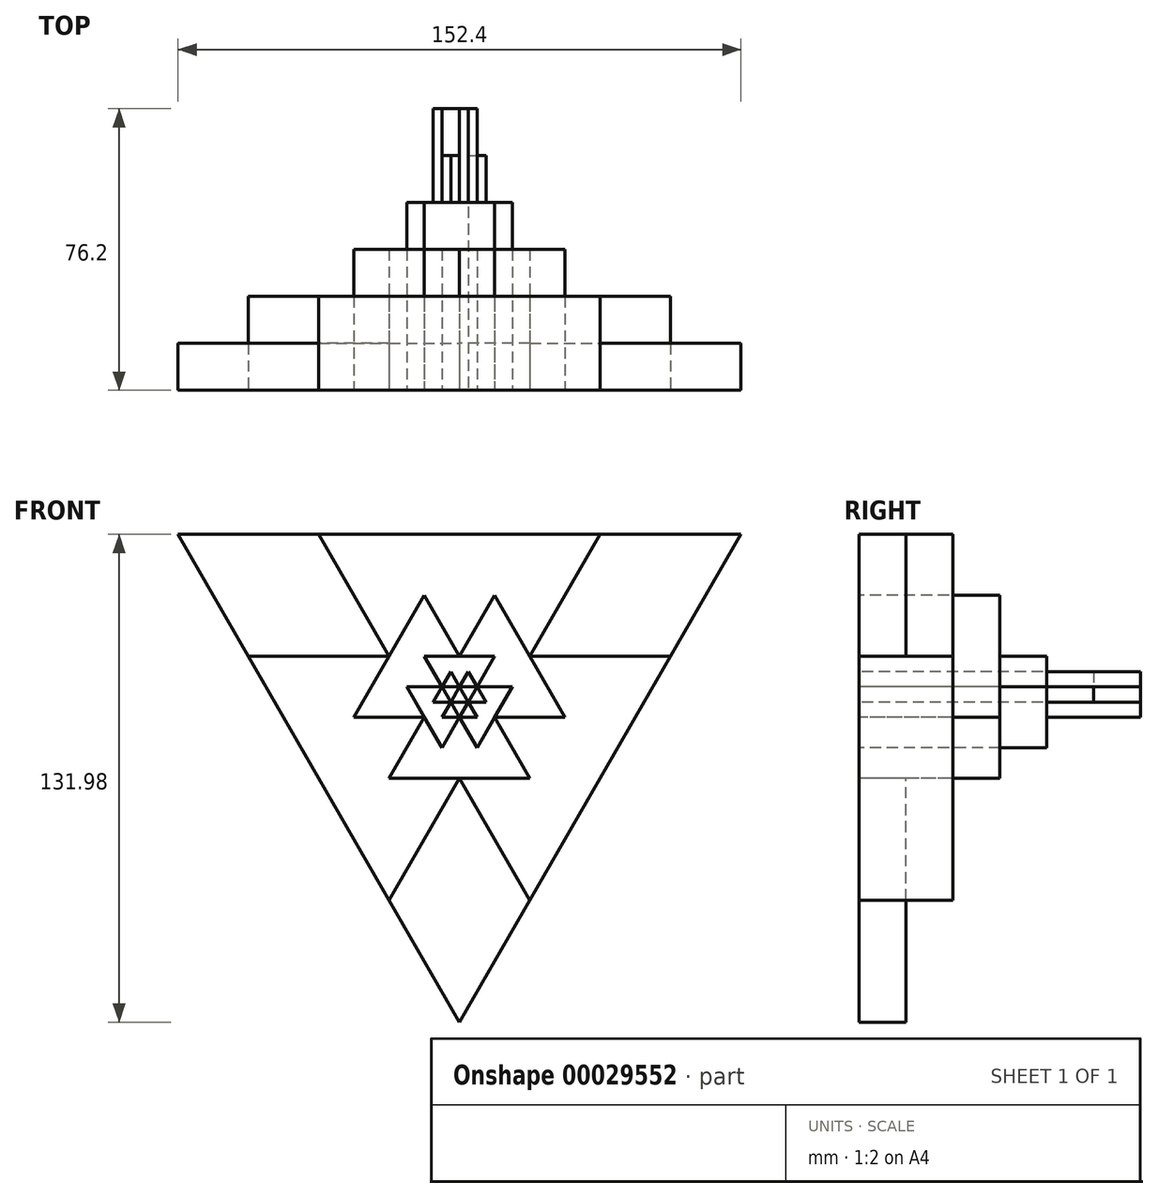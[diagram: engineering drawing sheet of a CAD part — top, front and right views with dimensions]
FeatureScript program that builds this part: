
annotation { "Feature Type Name" : "Feature", "Feature Type Description" : "" }
export const myFeature = defineFeature(function(context is Context, id is Id, definition is map)
    precondition{}
    {
        {
            var Q0;
            Q0=qCreatedBy(makeId("Front.planeOp"),FACE);
            var sketch = newSketch(context, id + "F0", { "sketchPlane" : qUnion([Q0])});
            skLineSegment(sketch, "E0.0", {"start": v(-76.2, 44) * mm, "end": v(76.2, 44) * mm});
            skLineSegment(sketch, "E0.1", {"start": v(76.2, 44) * mm, "end": v(0, -87.99) * mm});
            skLineSegment(sketch, "E0.2", {"start": v(0, -87.99) * mm, "end": v(-76.2, 44) * mm});
            skPoint(sketch, "E0.0.midPoint", {"position": v(0, 44) * mm});
            skLineSegment(sketch, "E1", {"start": v(-38.1, -22) * mm, "end": v(0, 44) * mm});
            skLineSegment(sketch, "E2", {"start": v(38.1, -22) * mm, "end": v(0, 44) * mm});
            skLineSegment(sketch, "E3", {"start": v(-38.1, -22) * mm, "end": v(38.1, -22) * mm});
            skLineSegment(sketch, "E4", {"start": v(0, -87.99) * mm, "end": v(-38.1, -22) * mm});
            skLineSegment(sketch, "E5", {"start": v(0, -87.99) * mm, "end": v(38.1, -22) * mm});
            skLineSegment(sketch, "E6", {"start": v(-76.2, 44) * mm, "end": v(-38.1, -22) * mm});
            skLineSegment(sketch, "E7", {"start": v(-76.2, 44) * mm, "end": v(0, 44) * mm});
            skLineSegment(sketch, "E8", {"start": v(0, 44) * mm, "end": v(76.2, 44) * mm});
            skLineSegment(sketch, "E9", {"start": v(38.1, -22) * mm, "end": v(76.2, 44) * mm});
            skPoint(sketch, "E0.cCircle.center.orphan", {"position": v(0, 0) * mm});
            skLineSegment(sketch, "E10", {"start": v(-19.05, 11) * mm, "end": v(19.05, 11) * mm});
            skLineSegment(sketch, "E11", {"start": v(0, -22) * mm, "end": v(19.05, 11) * mm});
            skLineSegment(sketch, "E12", {"start": v(-19.05, 11) * mm, "end": v(0, -22) * mm});
            skLineSegment(sketch, "E13", {"start": v(-9.52, -5.5) * mm, "end": v(-19.05, -22) * mm});
            skLineSegment(sketch, "E14", {"start": v(-9.52, -5.5) * mm, "end": v(-28.57, -5.5) * mm});
            skLineSegment(sketch, "E15", {"start": v(-28.57, -5.5) * mm, "end": v(-19.05, -22) * mm});
            skLineSegment(sketch, "E16", {"start": v(9.53, -5.5) * mm, "end": v(28.58, -5.5) * mm});
            skLineSegment(sketch, "E17", {"start": v(28.58, -5.5) * mm, "end": v(19.05, -22) * mm});
            skLineSegment(sketch, "E18", {"start": v(19.05, -22) * mm, "end": v(9.52, -5.5) * mm});
            skPoint(sketch, "E19.start.orphan", {"position": v(0, 11) * mm});
            skLineSegment(sketch, "E20", {"start": v(0, 11) * mm, "end": v(-9.52, 27.5) * mm});
            skLineSegment(sketch, "E21", {"start": v(-9.52, 27.5) * mm, "end": v(9.52, 27.5) * mm});
            skLineSegment(sketch, "E22", {"start": v(9.52, 27.5) * mm, "end": v(0, 11) * mm});
            skPoint(sketch, "E23.start.orphan", {"position": v(-9.52, -38.5) * mm});
            skPoint(sketch, "E24.end.orphan", {"position": v(9.53, -38.5) * mm});
            skPoint(sketch, "E24.start.orphan", {"position": v(0, -55) * mm});
            skPoint(sketch, "E25.end.orphan", {"position": v(-47.62, 27.5) * mm});
            skPoint(sketch, "E26.end.orphan", {"position": v(-28.57, 27.5) * mm});
            skPoint(sketch, "E26.start.orphan", {"position": v(-38.1, 11) * mm});
            skPoint(sketch, "E27.orphan", {"position": v(-57.15, 11) * mm});
            skPoint(sketch, "E28.orphan", {"position": v(-38.1, 44) * mm});
            skPoint(sketch, "E29.end.orphan", {"position": v(47.62, 27.5) * mm});
            skPoint(sketch, "E29.start.orphan", {"position": v(38.1, 11) * mm});
            skPoint(sketch, "E30.orphan", {"position": v(57.15, 11) * mm});
            skPoint(sketch, "E31.start.orphan", {"position": v(38.1, 44) * mm});
            skPoint(sketch, "E32.end.orphan", {"position": v(28.57, 27.5) * mm});
            skPoint(sketch, "E33.orphan", {"position": v(19.05, -55) * mm});
            skPoint(sketch, "E34.start.orphan", {"position": v(-19.05, -55) * mm});
            skLineSegment(sketch, "E35", {"start": v(-38.1, 44) * mm, "end": v(-57.15, 11) * mm});
            skLineSegment(sketch, "E36", {"start": v(-19.05, 11) * mm, "end": v(-57.15, 11) * mm});
            skLineSegment(sketch, "E37", {"start": v(-38.1, 44) * mm, "end": v(-19.05, 11) * mm});
            skLineSegment(sketch, "E38", {"start": v(19.05, 11) * mm, "end": v(38.1, 44) * mm});
            skLineSegment(sketch, "E39", {"start": v(57.15, 11) * mm, "end": v(38.1, 44) * mm});
            skLineSegment(sketch, "E40", {"start": v(19.05, 11) * mm, "end": v(57.15, 11) * mm});
            skLineSegment(sketch, "E41", {"start": v(-19.05, -55) * mm, "end": v(0, -22) * mm});
            skLineSegment(sketch, "E42", {"start": v(19.05, -55) * mm, "end": v(0, -22) * mm});
            skLineSegment(sketch, "E43", {"start": v(-19.05, -55) * mm, "end": v(19.05, -55) * mm});
            skLineSegment(sketch, "E44", {"start": v(-9.52, -5.5) * mm, "end": v(0, 11) * mm});
            skLineSegment(sketch, "E45", {"start": v(9.53, -5.5) * mm, "end": v(0, 11) * mm});
            skLineSegment(sketch, "E46", {"start": v(-9.52, -5.5) * mm, "end": v(9.53, -5.5) * mm});
            skLineSegment(sketch, "E47", {"start": v(-4.76, 2.75) * mm, "end": v(0, -5.5) * mm});
            skLineSegment(sketch, "E48", {"start": v(0, -5.5) * mm, "end": v(4.76, 2.75) * mm});
            skLineSegment(sketch, "E49", {"start": v(4.76, 2.75) * mm, "end": v(-4.76, 2.75) * mm});
            skLineSegment(sketch, "E50", {"start": v(0, -5.5) * mm, "end": v(4.76, -13.75) * mm});
            skLineSegment(sketch, "E51", {"start": v(4.76, -13.75) * mm, "end": v(-4.76, -13.75) * mm});
            skLineSegment(sketch, "E52", {"start": v(-4.76, -13.75) * mm, "end": v(0, -5.5) * mm});
            skLineSegment(sketch, "E53", {"start": v(-4.76, 2.75) * mm, "end": v(-9.52, 11) * mm});
            skLineSegment(sketch, "E54", {"start": v(-4.76, 2.75) * mm, "end": v(-14.29, 2.75) * mm});
            skLineSegment(sketch, "E55", {"start": v(-14.29, 2.75) * mm, "end": v(-9.52, 11) * mm});
            skLineSegment(sketch, "E56", {"start": v(4.76, 2.75) * mm, "end": v(14.29, 2.75) * mm});
            skLineSegment(sketch, "E57", {"start": v(4.76, 2.75) * mm, "end": v(9.53, 11) * mm});
            skLineSegment(sketch, "E58", {"start": v(9.53, 11) * mm, "end": v(14.29, 2.75) * mm});
            skLineSegment(sketch, "E59", {"start": v(-2.38, -1.37) * mm, "end": v(-4.76, -5.5) * mm});
            skLineSegment(sketch, "E60", {"start": v(-2.38, -1.37) * mm, "end": v(-7.14, -1.37) * mm});
            skLineSegment(sketch, "E61", {"start": v(-7.14, -1.37) * mm, "end": v(-4.76, -5.5) * mm});
            skLineSegment(sketch, "E62", {"start": v(2.38, -1.37) * mm, "end": v(7.14, -1.37) * mm});
            skLineSegment(sketch, "E63", {"start": v(7.14, -1.37) * mm, "end": v(4.76, -5.5) * mm});
            skLineSegment(sketch, "E64", {"start": v(4.76, -5.5) * mm, "end": v(2.38, -1.37) * mm});
            skLineSegment(sketch, "E65", {"start": v(0, 2.75) * mm, "end": v(2.38, 6.87) * mm});
            skLineSegment(sketch, "E66", {"start": v(2.38, 6.87) * mm, "end": v(-2.38, 6.87) * mm});
            skLineSegment(sketch, "E67", {"start": v(-2.38, 6.87) * mm, "end": v(0, 2.75) * mm});
            skLineSegment(sketch, "E68", {"start": v(0, 2.75) * mm, "end": v(-2.38, -1.37) * mm});
            skLineSegment(sketch, "E69", {"start": v(2.38, -1.37) * mm, "end": v(-2.38, -1.37) * mm});
            skLineSegment(sketch, "E70", {"start": v(2.38, -1.37) * mm, "end": v(0, 2.75) * mm});
            skSolve(sketch);
        }
        {
            var Q0;
            Q0=makeQuery(id+"F0.imprint","IMPRINT",FACE,{"disambiguationData":[TD([[makeQuery(id+"F0.imprint","IMPRINT",EDGE,{"derivedFrom":sQuery(id+"F0.wireOp",EDGE,"E68")}),1.0]])]});
            extrude(context, id + "F1", {"entities" : qUnion([Q0]), "oppositeDirection" : true, "depth" : 127 * mm});
        }
        {
            var Q0;
            {var subQ0=sQuery(id+"F0.wireOp",EDGE,"E69");Q0=makeQuery(id+"F0.imprint","IMPRINT",FACE,{"disambiguationData":[TD([[makeQuery(id+"F0.imprint","IMPRINT",EDGE,{"derivedFrom":subQ0}),1.0]])]});}
            var Q1;
            {var subQ0=sQuery(id+"F0.wireOp",EDGE,"E68");Q1=makeQuery(id+"F0.imprint","IMPRINT",FACE,{"disambiguationData":[TD([[makeQuery(id+"F0.imprint","IMPRINT",EDGE,{"derivedFrom":subQ0}),-1.0]])]});}
            var Q2;
            {var subQ0=sQuery(id+"F0.wireOp",EDGE,"E70");Q2=makeQuery(id+"F0.imprint","IMPRINT",FACE,{"disambiguationData":[TD([[makeQuery(id+"F0.imprint","IMPRINT",EDGE,{"derivedFrom":subQ0}),-1.0]])]});}
            extrude(context, id + "F2", {"entities" : qUnion([Q0, Q1, Q2]), "oppositeDirection" : true, "depth" : 114.3 * mm});
        }
        {
            var Q0;
            {var subQ0=sQuery(id+"F0.wireOp",EDGE,"E60");Q0=makeQuery(id+"F0.imprint","IMPRINT",FACE,{"disambiguationData":[TD([[makeQuery(id+"F0.imprint","IMPRINT",EDGE,{"derivedFrom":subQ0}),-1.0]])]});}
            var Q1;
            {var subQ0=sQuery(id+"F0.wireOp",EDGE,"E67");Q1=makeQuery(id+"F0.imprint","IMPRINT",FACE,{"disambiguationData":[TD([[makeQuery(id+"F0.imprint","IMPRINT",EDGE,{"derivedFrom":subQ0}),-1.0]])]});}
            var Q2;
            {var subQ0=sQuery(id+"F0.wireOp",EDGE,"E65");Q2=makeQuery(id+"F0.imprint","IMPRINT",FACE,{"disambiguationData":[TD([[makeQuery(id+"F0.imprint","IMPRINT",EDGE,{"derivedFrom":subQ0}),-1.0]])]});}
            var Q3;
            {var subQ0=sQuery(id+"F0.wireOp",EDGE,"E62");Q3=makeQuery(id+"F0.imprint","IMPRINT",FACE,{"disambiguationData":[TD([[makeQuery(id+"F0.imprint","IMPRINT",EDGE,{"derivedFrom":subQ0}),1.0]])]});}
            var Q4;
            {var subQ0=sQuery(id+"F0.wireOp",EDGE,"E64");Q4=makeQuery(id+"F0.imprint","IMPRINT",FACE,{"disambiguationData":[TD([[makeQuery(id+"F0.imprint","IMPRINT",EDGE,{"derivedFrom":subQ0}),1.0]])]});}
            var Q5;
            {var subQ1=sQuery(id+"F0.wireOp",EDGE,"E59");Q5=makeQuery(id+"F0.imprint","IMPRINT",FACE,{"disambiguationData":[TD([[makeQuery(id+"F0.imprint","IMPRINT",EDGE,{"derivedFrom":subQ1}),1.0]])]});}
            extrude(context, id + "F3", {"entities" : qUnion([Q0, Q1, Q2, Q3, Q4, Q5]), "oppositeDirection" : true, "depth" : 101.6 * mm});
        }
        {
            var Q0;
            Q0=makeQuery(id+"F0.imprint","IMPRINT",FACE,{"disambiguationData":[TD([[makeQuery(id+"F0.imprint","IMPRINT",EDGE,{"derivedFrom":sQuery(id+"F0.wireOp",EDGE,"E59")}),-1.0]])]});
            var Q1;
            {var subQ0=sQuery(id+"F0.wireOp",EDGE,"E54");Q1=makeQuery(id+"F0.imprint","IMPRINT",FACE,{"disambiguationData":[TD([[makeQuery(id+"F0.imprint","IMPRINT",EDGE,{"derivedFrom":subQ0}),1.0]])]});}
            var Q2;
            {var subQ0=sQuery(id+"F0.wireOp",EDGE,"E53");Q2=makeQuery(id+"F0.imprint","IMPRINT",FACE,{"disambiguationData":[TD([[makeQuery(id+"F0.imprint","IMPRINT",EDGE,{"derivedFrom":subQ0}),-1.0]])]});}
            var Q3;
            Q3=makeQuery(id+"F0.imprint","IMPRINT",FACE,{"disambiguationData":[TD([[makeQuery(id+"F0.imprint","IMPRINT",EDGE,{"derivedFrom":sQuery(id+"F0.wireOp",EDGE,"E65")}),1.0]])]});
            var Q4;
            {var subQ0=sQuery(id+"F0.wireOp",EDGE,"E57");Q4=makeQuery(id+"F0.imprint","IMPRINT",FACE,{"disambiguationData":[TD([[makeQuery(id+"F0.imprint","IMPRINT",EDGE,{"derivedFrom":subQ0}),1.0]])]});}
            var Q5;
            {var subQ2=sQuery(id+"F0.wireOp",EDGE,"E56");Q5=makeQuery(id+"F0.imprint","IMPRINT",FACE,{"disambiguationData":[TD([[makeQuery(id+"F0.imprint","IMPRINT",EDGE,{"derivedFrom":subQ2}),-1.0]])]});}
            var Q6;
            Q6=makeQuery(id+"F0.imprint","IMPRINT",FACE,{"disambiguationData":[TD([[makeQuery(id+"F0.imprint","IMPRINT",EDGE,{"derivedFrom":sQuery(id+"F0.wireOp",EDGE,"E62")}),-1.0]])]});
            var Q7;
            {var subQ0=sQuery(id+"F0.wireOp",EDGE,"E63");Q7=makeQuery(id+"F0.imprint","IMPRINT",FACE,{"disambiguationData":[TD([[makeQuery(id+"F0.imprint","IMPRINT",EDGE,{"derivedFrom":subQ0}),1.0]])]});}
            var Q8;
            {var subQ0=sQuery(id+"F0.wireOp",EDGE,"E61");Q8=makeQuery(id+"F0.imprint","IMPRINT",FACE,{"disambiguationData":[TD([[makeQuery(id+"F0.imprint","IMPRINT",EDGE,{"derivedFrom":subQ0}),-1.0]])]});}
            var Q9;
            {var subQ0=sQuery(id+"F0.wireOp",EDGE,"E66");Q9=makeQuery(id+"F0.imprint","IMPRINT",FACE,{"disambiguationData":[TD([[makeQuery(id+"F0.imprint","IMPRINT",EDGE,{"derivedFrom":subQ0}),-1.0]])]});}
            var Q10;
            {var subQ0=sQuery(id+"F0.wireOp",EDGE,"E52");Q10=makeQuery(id+"F0.imprint","IMPRINT",FACE,{"disambiguationData":[TD([[makeQuery(id+"F0.imprint","IMPRINT",EDGE,{"derivedFrom":subQ0}),1.0]])]});}
            var Q11;
            {var subQ0=sQuery(id+"F0.wireOp",EDGE,"E50");Q11=makeQuery(id+"F0.imprint","IMPRINT",FACE,{"disambiguationData":[TD([[makeQuery(id+"F0.imprint","IMPRINT",EDGE,{"derivedFrom":subQ0}),1.0]])]});}
            extrude(context, id + "F4", {"entities" : qUnion([Q0, Q1, Q2, Q3, Q4, Q5, Q6, Q7, Q8, Q9, Q10, Q11]), "oppositeDirection" : true, "depth" : 88.9 * mm});
        }
        {
            var Q0;
            Q0=makeQuery(id+"F0.imprint","IMPRINT",FACE,{"disambiguationData":[TD([[makeQuery(id+"F0.imprint","IMPRINT",EDGE,{"derivedFrom":sQuery(id+"F0.wireOp",EDGE,"E53")}),1.0]])]});
            var Q1;
            {var subQ0=sQuery(id+"F0.wireOp",EDGE,"E55");Q1=makeQuery(id+"F0.imprint","IMPRINT",FACE,{"disambiguationData":[TD([[makeQuery(id+"F0.imprint","IMPRINT",EDGE,{"derivedFrom":subQ0}),1.0]])]});}
            var Q2;
            {var subQ0=sQuery(id+"F0.wireOp",EDGE,"E14");Q2=makeQuery(id+"F0.imprint","IMPRINT",FACE,{"disambiguationData":[TD([[makeQuery(id+"F0.imprint","IMPRINT",EDGE,{"derivedFrom":subQ0}),-1.0]])]});}
            var Q3;
            {var subQ0=sQuery(id+"F0.wireOp",EDGE,"E20");Q3=makeQuery(id+"F0.imprint","IMPRINT",FACE,{"disambiguationData":[TD([[makeQuery(id+"F0.imprint","IMPRINT",EDGE,{"derivedFrom":subQ0}),1.0]])]});}
            var Q4;
            {var subQ0=sQuery(id+"F0.wireOp",EDGE,"E13");Q4=makeQuery(id+"F0.imprint","IMPRINT",FACE,{"disambiguationData":[TD([[makeQuery(id+"F0.imprint","IMPRINT",EDGE,{"derivedFrom":subQ0}),1.0]])]});}
            var Q5;
            {var subQ0=sQuery(id+"F0.wireOp",EDGE,"E51");Q5=makeQuery(id+"F0.imprint","IMPRINT",FACE,{"disambiguationData":[TD([[makeQuery(id+"F0.imprint","IMPRINT",EDGE,{"derivedFrom":subQ0}),1.0]])]});}
            var Q6;
            Q6=makeQuery(id+"F0.imprint","IMPRINT",FACE,{"disambiguationData":[TD([[makeQuery(id+"F0.imprint","IMPRINT",EDGE,{"derivedFrom":sQuery(id+"F0.wireOp",EDGE,"E50")}),-1.0]])]});
            var Q7;
            {var subQ0=sQuery(id+"F0.wireOp",EDGE,"E18");Q7=makeQuery(id+"F0.imprint","IMPRINT",FACE,{"disambiguationData":[TD([[makeQuery(id+"F0.imprint","IMPRINT",EDGE,{"derivedFrom":subQ0}),1.0]])]});}
            var Q8;
            {var subQ4=sQuery(id+"F0.wireOp",EDGE,"E16");Q8=makeQuery(id+"F0.imprint","IMPRINT",FACE,{"disambiguationData":[TD([[makeQuery(id+"F0.imprint","IMPRINT",EDGE,{"derivedFrom":subQ4}),1.0]])]});}
            var Q9;
            {var subQ0=sQuery(id+"F0.wireOp",EDGE,"E58");Q9=makeQuery(id+"F0.imprint","IMPRINT",FACE,{"disambiguationData":[TD([[makeQuery(id+"F0.imprint","IMPRINT",EDGE,{"derivedFrom":subQ0}),1.0]])]});}
            var Q10;
            Q10=makeQuery(id+"F0.imprint","IMPRINT",FACE,{"disambiguationData":[TD([[makeQuery(id+"F0.imprint","IMPRINT",EDGE,{"derivedFrom":sQuery(id+"F0.wireOp",EDGE,"E56")}),1.0]])]});
            var Q11;
            {var subQ0=sQuery(id+"F0.wireOp",EDGE,"E22");Q11=makeQuery(id+"F0.imprint","IMPRINT",FACE,{"disambiguationData":[TD([[makeQuery(id+"F0.imprint","IMPRINT",EDGE,{"derivedFrom":subQ0}),1.0]])]});}
            extrude(context, id + "F5", {"entities" : qUnion([Q0, Q1, Q2, Q3, Q4, Q5, Q6, Q7, Q8, Q9, Q10, Q11]), "oppositeDirection" : true, "depth" : 76.2 * mm});
        }
        {
            var Q0;
            Q0=makeQuery(id+"F0.imprint","IMPRINT",FACE,{"disambiguationData":[TD([[makeQuery(id+"F0.imprint","IMPRINT",EDGE,{"derivedFrom":sQuery(id+"F0.wireOp",EDGE,"E13")}),-1.0]])]});
            var Q1;
            {var subQ0=sQuery(id+"F0.wireOp",EDGE,"E41");Q1=makeQuery(id+"F0.imprint","IMPRINT",FACE,{"disambiguationData":[TD([[makeQuery(id+"F0.imprint","IMPRINT",EDGE,{"derivedFrom":subQ0}),1.0]])]});}
            var Q2;
            {var subQ0=sQuery(id+"F0.wireOp",EDGE,"E15");Q2=makeQuery(id+"F0.imprint","IMPRINT",FACE,{"disambiguationData":[TD([[makeQuery(id+"F0.imprint","IMPRINT",EDGE,{"derivedFrom":subQ0}),-1.0]])]});}
            var Q3;
            {var subQ0=sQuery(id+"F0.wireOp",EDGE,"E36");Q3=makeQuery(id+"F0.imprint","IMPRINT",FACE,{"disambiguationData":[TD([[makeQuery(id+"F0.imprint","IMPRINT",EDGE,{"derivedFrom":subQ0}),1.0]])]});}
            var Q4;
            {var subQ0=sQuery(id+"F0.wireOp",EDGE,"E37");Q4=makeQuery(id+"F0.imprint","IMPRINT",FACE,{"disambiguationData":[TD([[makeQuery(id+"F0.imprint","IMPRINT",EDGE,{"derivedFrom":subQ0}),1.0]])]});}
            var Q5;
            Q5=makeQuery(id+"F0.imprint","IMPRINT",FACE,{"disambiguationData":[TD([[makeQuery(id+"F0.imprint","IMPRINT",EDGE,{"derivedFrom":sQuery(id+"F0.wireOp",EDGE,"E20")}),-1.0]])]});
            var Q6;
            {var subQ0=sQuery(id+"F0.wireOp",EDGE,"E21");Q6=makeQuery(id+"F0.imprint","IMPRINT",FACE,{"disambiguationData":[TD([[makeQuery(id+"F0.imprint","IMPRINT",EDGE,{"derivedFrom":subQ0}),1.0]])]});}
            var Q7;
            {var subQ0=sQuery(id+"F0.wireOp",EDGE,"E38");Q7=makeQuery(id+"F0.imprint","IMPRINT",FACE,{"disambiguationData":[TD([[makeQuery(id+"F0.imprint","IMPRINT",EDGE,{"derivedFrom":subQ0}),1.0]])]});}
            var Q8;
            {var subQ0=sQuery(id+"F0.wireOp",EDGE,"E40");Q8=makeQuery(id+"F0.imprint","IMPRINT",FACE,{"disambiguationData":[TD([[makeQuery(id+"F0.imprint","IMPRINT",EDGE,{"derivedFrom":subQ0}),-1.0]])]});}
            var Q9;
            {var subQ0=sQuery(id+"F0.wireOp",EDGE,"E42");Q9=makeQuery(id+"F0.imprint","IMPRINT",FACE,{"disambiguationData":[TD([[makeQuery(id+"F0.imprint","IMPRINT",EDGE,{"derivedFrom":subQ0}),-1.0]])]});}
            var Q10;
            {var subQ1=sQuery(id+"F0.wireOp",EDGE,"E17");Q10=makeQuery(id+"F0.imprint","IMPRINT",FACE,{"disambiguationData":[TD([[makeQuery(id+"F0.imprint","IMPRINT",EDGE,{"derivedFrom":subQ1}),1.0]])]});}
            var Q11;
            Q11=makeQuery(id+"F0.imprint","IMPRINT",FACE,{"disambiguationData":[TD([[makeQuery(id+"F0.imprint","IMPRINT",EDGE,{"derivedFrom":sQuery(id+"F0.wireOp",EDGE,"E16")}),-1.0]])]});
            extrude(context, id + "F6", {"entities" : qUnion([Q0, Q1, Q2, Q3, Q4, Q5, Q6, Q7, Q8, Q9, Q10, Q11]), "oppositeDirection" : true, "depth" : 63.5 * mm});
        }
        {
            var Q0;
            Q0=makeQuery(id+"F0.imprint","IMPRINT",FACE,{"disambiguationData":[TD([[makeQuery(id+"F0.imprint","IMPRINT",EDGE,{"derivedFrom":sQuery(id+"F0.wireOp",EDGE,"E41")}),-1.0]])]});
            var Q1;
            {var subQ1=sQuery(id+"F0.wireOp",EDGE,"E43");Q1=makeQuery(id+"F0.imprint","IMPRINT",FACE,{"disambiguationData":[TD([[makeQuery(id+"F0.imprint","IMPRINT",EDGE,{"derivedFrom":subQ1}),-1.0]])]});}
            var Q2;
            Q2=makeQuery(id+"F0.imprint","IMPRINT",FACE,{"disambiguationData":[TD([[makeQuery(id+"F0.imprint","IMPRINT",EDGE,{"derivedFrom":sQuery(id+"F0.wireOp",EDGE,"E35")}),1.0]])]});
            var Q3;
            {var subQ0=sQuery(id+"F0.wireOp",EDGE,"E35");Q3=makeQuery(id+"F0.imprint","IMPRINT",FACE,{"disambiguationData":[TD([[makeQuery(id+"F0.imprint","IMPRINT",EDGE,{"derivedFrom":subQ0}),-1.0]])]});}
            var Q4;
            {var subQ0=sQuery(id+"F0.wireOp",EDGE,"E39");Q4=makeQuery(id+"F0.imprint","IMPRINT",FACE,{"disambiguationData":[TD([[makeQuery(id+"F0.imprint","IMPRINT",EDGE,{"derivedFrom":subQ0}),-1.0]])]});}
            var Q5;
            Q5=makeQuery(id+"F0.imprint","IMPRINT",FACE,{"disambiguationData":[TD([[makeQuery(id+"F0.imprint","IMPRINT",EDGE,{"derivedFrom":sQuery(id+"F0.wireOp",EDGE,"E38")}),-1.0]])]});
            extrude(context, id + "F7", {"entities" : qUnion([Q0, Q1, Q2, Q3, Q4, Q5]), "oppositeDirection" : true, "depth" : 50.8 * mm});
        }
        {
            var Q0;
            Q0=makeQuery(id+"F2.opExtrude","CAP_FACE",FACE,{"disambiguationData":[OSD([sQuery(id+"F0.wireOp",EDGE,"E47"),sQuery(id+"F0.wireOp",EDGE,"E49"),sQuery(id+"F0.wireOp",EDGE,"E68")])],"isStart":false});
            var Q1;
            Q1=makeQuery(id+"F2.opExtrude","CAP_FACE",FACE,{"disambiguationData":[OSD([sQuery(id+"F0.wireOp",EDGE,"E47"),sQuery(id+"F0.wireOp",EDGE,"E48"),sQuery(id+"F0.wireOp",EDGE,"E69")])],"isStart":false});
            var Q2;
            Q2=makeQuery(id+"F2.opExtrude","CAP_FACE",FACE,{"disambiguationData":[OSD([sQuery(id+"F0.wireOp",EDGE,"E48"),sQuery(id+"F0.wireOp",EDGE,"E49"),sQuery(id+"F0.wireOp",EDGE,"E70")])],"isStart":false});
            extrude(context, id + "F8", {"entities" : qUnion([Q0, Q1, Q2]), "operationType" : NewBodyOperationType.REMOVE, "oppositeDirection" : true, "depth" : 12.7 * mm});
        }
        {
            var Q0;
            Q0=makeQuery(id+"F1.opExtrude","CAP_FACE",FACE,{"disambiguationData":[OSD([sQuery(id+"F0.wireOp",EDGE,"E68"),sQuery(id+"F0.wireOp",EDGE,"E69"),sQuery(id+"F0.wireOp",EDGE,"E70")])],"isStart":false});
            extrude(context, id + "F9", {"entities" : qUnion([Q0]), "operationType" : NewBodyOperationType.REMOVE, "oppositeDirection" : true, "depth" : 12.7 * mm});
        }
        {
            var Q0;
            Q0=makeQuery(id+"F6.opExtrude","CAP_FACE",FACE,{"disambiguationData":[OSD([sQuery(id+"F0.wireOp",EDGE,"E2"),sQuery(id+"F0.wireOp",EDGE,"E3"),sQuery(id+"F0.wireOp",EDGE,"E5"),sQuery(id+"F0.wireOp",EDGE,"E9"),sQuery(id+"F0.wireOp",EDGE,"E16"),sQuery(id+"F0.wireOp",EDGE,"E18"),sQuery(id+"F0.wireOp",EDGE,"E40"),sQuery(id+"F0.wireOp",EDGE,"E42")])],"isStart":false});
            var Q1;
            Q1=makeQuery(id+"F6.opExtrude","CAP_FACE",FACE,{"disambiguationData":[OSD([sQuery(id+"F0.wireOp",EDGE,"E1"),sQuery(id+"F0.wireOp",EDGE,"E3"),sQuery(id+"F0.wireOp",EDGE,"E4"),sQuery(id+"F0.wireOp",EDGE,"E6"),sQuery(id+"F0.wireOp",EDGE,"E13"),sQuery(id+"F0.wireOp",EDGE,"E14"),sQuery(id+"F0.wireOp",EDGE,"E36"),sQuery(id+"F0.wireOp",EDGE,"E41")])],"isStart":false});
            var Q2;
            Q2=makeQuery(id+"F7.opExtrude","CAP_FACE",FACE,{"disambiguationData":[OSD([sQuery(id+"F0.wireOp",EDGE,"E6"),sQuery(id+"F0.wireOp",EDGE,"E7"),sQuery(id+"F0.wireOp",EDGE,"E36"),sQuery(id+"F0.wireOp",EDGE,"E37")])],"isStart":false});
            var Q3;
            Q3=makeQuery(id+"F6.opExtrude","CAP_FACE",FACE,{"disambiguationData":[OSD([sQuery(id+"F0.wireOp",EDGE,"E1"),sQuery(id+"F0.wireOp",EDGE,"E2"),sQuery(id+"F0.wireOp",EDGE,"E7"),sQuery(id+"F0.wireOp",EDGE,"E8"),sQuery(id+"F0.wireOp",EDGE,"E20"),sQuery(id+"F0.wireOp",EDGE,"E22"),sQuery(id+"F0.wireOp",EDGE,"E37"),sQuery(id+"F0.wireOp",EDGE,"E38")])],"isStart":false});
            var Q4;
            Q4=makeQuery(id+"F7.opExtrude","CAP_FACE",FACE,{"disambiguationData":[OSD([sQuery(id+"F0.wireOp",EDGE,"E8"),sQuery(id+"F0.wireOp",EDGE,"E9"),sQuery(id+"F0.wireOp",EDGE,"E38"),sQuery(id+"F0.wireOp",EDGE,"E40")])],"isStart":false});
            var Q5;
            Q5=makeQuery(id+"F5.opExtrude","CAP_FACE",FACE,{"disambiguationData":[OSD([sQuery(id+"F0.wireOp",EDGE,"E1"),sQuery(id+"F0.wireOp",EDGE,"E10"),sQuery(id+"F0.wireOp",EDGE,"E12"),sQuery(id+"F0.wireOp",EDGE,"E14"),sQuery(id+"F0.wireOp",EDGE,"E20"),sQuery(id+"F0.wireOp",EDGE,"E53"),sQuery(id+"F0.wireOp",EDGE,"E54")])],"isStart":false});
            var Q6;
            Q6=makeQuery(id+"F5.opExtrude","CAP_FACE",FACE,{"disambiguationData":[OSD([sQuery(id+"F0.wireOp",EDGE,"E2"),sQuery(id+"F0.wireOp",EDGE,"E10"),sQuery(id+"F0.wireOp",EDGE,"E11"),sQuery(id+"F0.wireOp",EDGE,"E16"),sQuery(id+"F0.wireOp",EDGE,"E22"),sQuery(id+"F0.wireOp",EDGE,"E56"),sQuery(id+"F0.wireOp",EDGE,"E57")])],"isStart":false});
            var Q7;
            Q7=makeQuery(id+"F5.opExtrude","CAP_FACE",FACE,{"disambiguationData":[OSD([sQuery(id+"F0.wireOp",EDGE,"E3"),sQuery(id+"F0.wireOp",EDGE,"E11"),sQuery(id+"F0.wireOp",EDGE,"E12"),sQuery(id+"F0.wireOp",EDGE,"E13"),sQuery(id+"F0.wireOp",EDGE,"E18"),sQuery(id+"F0.wireOp",EDGE,"E50"),sQuery(id+"F0.wireOp",EDGE,"E52")])],"isStart":false});
            var Q8;
            Q8=makeQuery(id+"F4.opExtrude","CAP_FACE",FACE,{"disambiguationData":[OSD([sQuery(id+"F0.wireOp",EDGE,"E12"),sQuery(id+"F0.wireOp",EDGE,"E44"),sQuery(id+"F0.wireOp",EDGE,"E46"),sQuery(id+"F0.wireOp",EDGE,"E52"),sQuery(id+"F0.wireOp",EDGE,"E54"),sQuery(id+"F0.wireOp",EDGE,"E59"),sQuery(id+"F0.wireOp",EDGE,"E60")])],"isStart":false});
            var Q9;
            Q9=makeQuery(id+"F4.opExtrude","CAP_FACE",FACE,{"disambiguationData":[OSD([sQuery(id+"F0.wireOp",EDGE,"E11"),sQuery(id+"F0.wireOp",EDGE,"E45"),sQuery(id+"F0.wireOp",EDGE,"E46"),sQuery(id+"F0.wireOp",EDGE,"E50"),sQuery(id+"F0.wireOp",EDGE,"E56"),sQuery(id+"F0.wireOp",EDGE,"E62"),sQuery(id+"F0.wireOp",EDGE,"E64")])],"isStart":false});
            var Q10;
            Q10=makeQuery(id+"F4.opExtrude","CAP_FACE",FACE,{"disambiguationData":[OSD([sQuery(id+"F0.wireOp",EDGE,"E10"),sQuery(id+"F0.wireOp",EDGE,"E44"),sQuery(id+"F0.wireOp",EDGE,"E45"),sQuery(id+"F0.wireOp",EDGE,"E53"),sQuery(id+"F0.wireOp",EDGE,"E57"),sQuery(id+"F0.wireOp",EDGE,"E65"),sQuery(id+"F0.wireOp",EDGE,"E67")])],"isStart":false});
            var Q11;
            Q11=makeQuery(id+"F3.opExtrude","CAP_FACE",FACE,{"disambiguationData":[OSD([sQuery(id+"F0.wireOp",EDGE,"E46"),sQuery(id+"F0.wireOp",EDGE,"E48"),sQuery(id+"F0.wireOp",EDGE,"E64")])],"isStart":false});
            var Q12;
            Q12=makeQuery(id+"F8.boolean.opBoolean","COPY",FACE,{"derivedFrom":makeQuery(id+"F8.opExtrude","CAP_FACE",FACE,{"disambiguationData":[OSD([sQuery(id+"F0.wireOp",EDGE,"E47"),sQuery(id+"F0.wireOp",EDGE,"E48"),sQuery(id+"F0.wireOp",EDGE,"E69")])],"isStart":false})});
            var Q13;
            Q13=makeQuery(id+"F3.opExtrude","CAP_FACE",FACE,{"disambiguationData":[OSD([sQuery(id+"F0.wireOp",EDGE,"E46"),sQuery(id+"F0.wireOp",EDGE,"E47"),sQuery(id+"F0.wireOp",EDGE,"E59")])],"isStart":false});
            var Q14;
            Q14=makeQuery(id+"F8.boolean.opBoolean","COPY",FACE,{"derivedFrom":makeQuery(id+"F8.opExtrude","CAP_FACE",FACE,{"disambiguationData":[OSD([sQuery(id+"F0.wireOp",EDGE,"E47"),sQuery(id+"F0.wireOp",EDGE,"E49"),sQuery(id+"F0.wireOp",EDGE,"E68")])],"isStart":false})});
            var Q15;
            Q15=makeQuery(id+"F3.opExtrude","CAP_FACE",FACE,{"disambiguationData":[OSD([sQuery(id+"F0.wireOp",EDGE,"E44"),sQuery(id+"F0.wireOp",EDGE,"E47"),sQuery(id+"F0.wireOp",EDGE,"E60")])],"isStart":false});
            var Q16;
            Q16=makeQuery(id+"F3.opExtrude","CAP_FACE",FACE,{"disambiguationData":[OSD([sQuery(id+"F0.wireOp",EDGE,"E44"),sQuery(id+"F0.wireOp",EDGE,"E49"),sQuery(id+"F0.wireOp",EDGE,"E67")])],"isStart":false});
            var Q17;
            Q17=makeQuery(id+"F3.opExtrude","CAP_FACE",FACE,{"disambiguationData":[OSD([sQuery(id+"F0.wireOp",EDGE,"E45"),sQuery(id+"F0.wireOp",EDGE,"E48"),sQuery(id+"F0.wireOp",EDGE,"E62")])],"isStart":false});
            var Q18;
            Q18=makeQuery(id+"F9.boolean.opBoolean","COPY",FACE,{"derivedFrom":makeQuery(id+"F9.opExtrude","CAP_FACE",FACE,{"disambiguationData":[OSD([sQuery(id+"F0.wireOp",EDGE,"E68"),sQuery(id+"F0.wireOp",EDGE,"E69"),sQuery(id+"F0.wireOp",EDGE,"E70")])],"isStart":false})});
            var Q19;
            Q19=makeQuery(id+"F8.boolean.opBoolean","COPY",FACE,{"derivedFrom":makeQuery(id+"F8.opExtrude","CAP_FACE",FACE,{"disambiguationData":[OSD([sQuery(id+"F0.wireOp",EDGE,"E48"),sQuery(id+"F0.wireOp",EDGE,"E49"),sQuery(id+"F0.wireOp",EDGE,"E70")])],"isStart":false})});
            var Q20;
            Q20=makeQuery(id+"F3.opExtrude","CAP_FACE",FACE,{"disambiguationData":[OSD([sQuery(id+"F0.wireOp",EDGE,"E45"),sQuery(id+"F0.wireOp",EDGE,"E49"),sQuery(id+"F0.wireOp",EDGE,"E65")])],"isStart":false});
            extrude(context, id + "F10", {"entities" : qUnion([Q0, Q1, Q2, Q3, Q4, Q5, Q6, Q7, Q8, Q9, Q10, Q11, Q12, Q13, Q14, Q15, Q16, Q17, Q18, Q19, Q20]), "operationType" : NewBodyOperationType.REMOVE, "oppositeDirection" : true, "depth" : 25.4 * mm});
        }
        {
            var Q0;
            Q0=makeQuery(id+"F7.opExtrude","CAP_FACE",FACE,{"disambiguationData":[OSD([sQuery(id+"F0.wireOp",EDGE,"E4"),sQuery(id+"F0.wireOp",EDGE,"E5"),sQuery(id+"F0.wireOp",EDGE,"E41"),sQuery(id+"F0.wireOp",EDGE,"E42")])],"isStart":false});
            extrude(context, id + "F11", {"entities" : qUnion([Q0]), "operationType" : NewBodyOperationType.REMOVE, "oppositeDirection" : true, "depth" : 25.4 * mm});
        }
        {
            var Q0;
            Q0=makeQuery(id+"F11.boolean.opBoolean","COPY",FACE,{"derivedFrom":makeQuery(id+"F11.opExtrude","CAP_FACE",FACE,{"disambiguationData":[OSD([sQuery(id+"F0.wireOp",EDGE,"E4"),sQuery(id+"F0.wireOp",EDGE,"E5"),sQuery(id+"F0.wireOp",EDGE,"E41"),sQuery(id+"F0.wireOp",EDGE,"E42")])],"isStart":false})});
            var Q1;
            Q1=makeQuery(id+"F10.boolean.opBoolean","COPY",FACE,{"derivedFrom":makeQuery(id+"F10.opExtrude","CAP_FACE",FACE,{"disambiguationData":[OSD([sQuery(id+"F0.wireOp",EDGE,"E2"),sQuery(id+"F0.wireOp",EDGE,"E3"),sQuery(id+"F0.wireOp",EDGE,"E5"),sQuery(id+"F0.wireOp",EDGE,"E9"),sQuery(id+"F0.wireOp",EDGE,"E16"),sQuery(id+"F0.wireOp",EDGE,"E18"),sQuery(id+"F0.wireOp",EDGE,"E40"),sQuery(id+"F0.wireOp",EDGE,"E42")])],"isStart":false})});
            var Q2;
            Q2=makeQuery(id+"F10.boolean.opBoolean","COPY",FACE,{"derivedFrom":makeQuery(id+"F10.opExtrude","CAP_FACE",FACE,{"disambiguationData":[OSD([sQuery(id+"F0.wireOp",EDGE,"E8"),sQuery(id+"F0.wireOp",EDGE,"E9"),sQuery(id+"F0.wireOp",EDGE,"E38"),sQuery(id+"F0.wireOp",EDGE,"E40")])],"isStart":false})});
            var Q3;
            Q3=makeQuery(id+"F10.boolean.opBoolean","COPY",FACE,{"derivedFrom":makeQuery(id+"F10.opExtrude","CAP_FACE",FACE,{"disambiguationData":[OSD([sQuery(id+"F0.wireOp",EDGE,"E1"),sQuery(id+"F0.wireOp",EDGE,"E3"),sQuery(id+"F0.wireOp",EDGE,"E4"),sQuery(id+"F0.wireOp",EDGE,"E6"),sQuery(id+"F0.wireOp",EDGE,"E13"),sQuery(id+"F0.wireOp",EDGE,"E14"),sQuery(id+"F0.wireOp",EDGE,"E36"),sQuery(id+"F0.wireOp",EDGE,"E41")])],"isStart":false})});
            var Q4;
            Q4=makeQuery(id+"F10.boolean.opBoolean","COPY",FACE,{"derivedFrom":makeQuery(id+"F10.opExtrude","CAP_FACE",FACE,{"disambiguationData":[OSD([sQuery(id+"F0.wireOp",EDGE,"E1"),sQuery(id+"F0.wireOp",EDGE,"E2"),sQuery(id+"F0.wireOp",EDGE,"E7"),sQuery(id+"F0.wireOp",EDGE,"E8"),sQuery(id+"F0.wireOp",EDGE,"E20"),sQuery(id+"F0.wireOp",EDGE,"E22"),sQuery(id+"F0.wireOp",EDGE,"E37"),sQuery(id+"F0.wireOp",EDGE,"E38")])],"isStart":false})});
            var Q5;
            Q5=makeQuery(id+"F10.boolean.opBoolean","COPY",FACE,{"derivedFrom":makeQuery(id+"F10.opExtrude","CAP_FACE",FACE,{"disambiguationData":[OSD([sQuery(id+"F0.wireOp",EDGE,"E6"),sQuery(id+"F0.wireOp",EDGE,"E7"),sQuery(id+"F0.wireOp",EDGE,"E36"),sQuery(id+"F0.wireOp",EDGE,"E37")])],"isStart":false})});
            var Q6;
            Q6=makeQuery(id+"F10.boolean.opBoolean","COPY",FACE,{"derivedFrom":makeQuery(id+"F10.opExtrude","CAP_FACE",FACE,{"disambiguationData":[OSD([sQuery(id+"F0.wireOp",EDGE,"E2"),sQuery(id+"F0.wireOp",EDGE,"E10"),sQuery(id+"F0.wireOp",EDGE,"E11"),sQuery(id+"F0.wireOp",EDGE,"E16"),sQuery(id+"F0.wireOp",EDGE,"E22"),sQuery(id+"F0.wireOp",EDGE,"E56"),sQuery(id+"F0.wireOp",EDGE,"E57")])],"isStart":false})});
            var Q7;
            Q7=makeQuery(id+"F10.boolean.opBoolean","COPY",FACE,{"derivedFrom":makeQuery(id+"F10.opExtrude","CAP_FACE",FACE,{"disambiguationData":[OSD([sQuery(id+"F0.wireOp",EDGE,"E1"),sQuery(id+"F0.wireOp",EDGE,"E10"),sQuery(id+"F0.wireOp",EDGE,"E12"),sQuery(id+"F0.wireOp",EDGE,"E14"),sQuery(id+"F0.wireOp",EDGE,"E20"),sQuery(id+"F0.wireOp",EDGE,"E53"),sQuery(id+"F0.wireOp",EDGE,"E54")])],"isStart":false})});
            var Q8;
            Q8=makeQuery(id+"F10.boolean.opBoolean","COPY",FACE,{"derivedFrom":makeQuery(id+"F10.opExtrude","CAP_FACE",FACE,{"disambiguationData":[OSD([sQuery(id+"F0.wireOp",EDGE,"E3"),sQuery(id+"F0.wireOp",EDGE,"E11"),sQuery(id+"F0.wireOp",EDGE,"E12"),sQuery(id+"F0.wireOp",EDGE,"E13"),sQuery(id+"F0.wireOp",EDGE,"E18"),sQuery(id+"F0.wireOp",EDGE,"E50"),sQuery(id+"F0.wireOp",EDGE,"E52")])],"isStart":false})});
            var Q9;
            Q9=makeQuery(id+"F10.boolean.opBoolean","COPY",FACE,{"derivedFrom":makeQuery(id+"F10.opExtrude","CAP_FACE",FACE,{"disambiguationData":[OSD([sQuery(id+"F0.wireOp",EDGE,"E11"),sQuery(id+"F0.wireOp",EDGE,"E45"),sQuery(id+"F0.wireOp",EDGE,"E46"),sQuery(id+"F0.wireOp",EDGE,"E50"),sQuery(id+"F0.wireOp",EDGE,"E56"),sQuery(id+"F0.wireOp",EDGE,"E62"),sQuery(id+"F0.wireOp",EDGE,"E64")])],"isStart":false})});
            var Q10;
            Q10=makeQuery(id+"F10.boolean.opBoolean","COPY",FACE,{"derivedFrom":makeQuery(id+"F10.opExtrude","CAP_FACE",FACE,{"disambiguationData":[OSD([sQuery(id+"F0.wireOp",EDGE,"E10"),sQuery(id+"F0.wireOp",EDGE,"E44"),sQuery(id+"F0.wireOp",EDGE,"E45"),sQuery(id+"F0.wireOp",EDGE,"E53"),sQuery(id+"F0.wireOp",EDGE,"E57"),sQuery(id+"F0.wireOp",EDGE,"E65"),sQuery(id+"F0.wireOp",EDGE,"E67")])],"isStart":false})});
            var Q11;
            Q11=makeQuery(id+"F10.boolean.opBoolean","COPY",FACE,{"derivedFrom":makeQuery(id+"F10.opExtrude","CAP_FACE",FACE,{"disambiguationData":[OSD([sQuery(id+"F0.wireOp",EDGE,"E12"),sQuery(id+"F0.wireOp",EDGE,"E44"),sQuery(id+"F0.wireOp",EDGE,"E46"),sQuery(id+"F0.wireOp",EDGE,"E52"),sQuery(id+"F0.wireOp",EDGE,"E54"),sQuery(id+"F0.wireOp",EDGE,"E59"),sQuery(id+"F0.wireOp",EDGE,"E60")])],"isStart":false})});
            var Q12;
            {var subQ0=sQuery(id+"F0.wireOp",EDGE,"E49");Q12=makeQuery(id+"F10.boolean.opBoolean","TWEAK_FACE",FACE,{"disambiguationData":[OD(1.0)],"derivedFrom":[makeQuery(id+"F10.opExtrude","CAP_FACE",FACE,{"disambiguationData":[OSD([sQuery(id+"F0.wireOp",EDGE,"E45"),subQ0,sQuery(id+"F0.wireOp",EDGE,"E65")])],"isStart":false}),makeQuery(id+"F10.opExtrude","CAP_FACE",FACE,{"disambiguationData":[OSD([sQuery(id+"F0.wireOp",EDGE,"E48"),subQ0,sQuery(id+"F0.wireOp",EDGE,"E70")])],"isStart":false})]});}
            var Q13;
            {var subQ0=sQuery(id+"F0.wireOp",EDGE,"E49");Q13=makeQuery(id+"F10.boolean.opBoolean","TWEAK_FACE",FACE,{"disambiguationData":[OD(0.0)],"derivedFrom":[makeQuery(id+"F10.opExtrude","CAP_FACE",FACE,{"disambiguationData":[OSD([sQuery(id+"F0.wireOp",EDGE,"E45"),subQ0,sQuery(id+"F0.wireOp",EDGE,"E65")])],"isStart":false}),makeQuery(id+"F10.opExtrude","CAP_FACE",FACE,{"disambiguationData":[OSD([sQuery(id+"F0.wireOp",EDGE,"E48"),subQ0,sQuery(id+"F0.wireOp",EDGE,"E70")])],"isStart":false})]});}
            var Q14;
            Q14=makeQuery(id+"F10.boolean.opBoolean","COPY",FACE,{"derivedFrom":makeQuery(id+"F10.opExtrude","CAP_FACE",FACE,{"disambiguationData":[OSD([sQuery(id+"F0.wireOp",EDGE,"E45"),sQuery(id+"F0.wireOp",EDGE,"E48"),sQuery(id+"F0.wireOp",EDGE,"E62")])],"isStart":false})});
            var Q15;
            {var subQ0=sQuery(id+"F0.wireOp",EDGE,"E48");var subQ1=sQuery(id+"F0.wireOp",EDGE,"E47");var subQ2=sQuery(id+"F0.wireOp",EDGE,"E46");Q15=makeQuery(id+"F10.boolean.opBoolean","TWEAK_FACE",FACE,{"disambiguationData":[OD(1.0)],"derivedFrom":[makeQuery(id+"F10.opExtrude","CAP_FACE",FACE,{"disambiguationData":[OSD([subQ2,subQ1,sQuery(id+"F0.wireOp",EDGE,"E59")])],"isStart":false}),makeQuery(id+"F10.opExtrude","CAP_FACE",FACE,{"disambiguationData":[OSD([subQ2,subQ0,sQuery(id+"F0.wireOp",EDGE,"E64")])],"isStart":false}),makeQuery(id+"F10.opExtrude","CAP_FACE",FACE,{"disambiguationData":[OSD([subQ1,subQ0,sQuery(id+"F0.wireOp",EDGE,"E69")])],"isStart":false})]});}
            var Q16;
            {var subQ0=sQuery(id+"F0.wireOp",EDGE,"E48");var subQ1=sQuery(id+"F0.wireOp",EDGE,"E47");var subQ2=sQuery(id+"F0.wireOp",EDGE,"E46");Q16=makeQuery(id+"F10.boolean.opBoolean","TWEAK_FACE",FACE,{"disambiguationData":[OD(0.0)],"derivedFrom":[makeQuery(id+"F10.opExtrude","CAP_FACE",FACE,{"disambiguationData":[OSD([subQ2,subQ1,sQuery(id+"F0.wireOp",EDGE,"E59")])],"isStart":false}),makeQuery(id+"F10.opExtrude","CAP_FACE",FACE,{"disambiguationData":[OSD([subQ2,subQ0,sQuery(id+"F0.wireOp",EDGE,"E64")])],"isStart":false}),makeQuery(id+"F10.opExtrude","CAP_FACE",FACE,{"disambiguationData":[OSD([subQ1,subQ0,sQuery(id+"F0.wireOp",EDGE,"E69")])],"isStart":false})]});}
            var Q17;
            {var subQ0=sQuery(id+"F0.wireOp",EDGE,"E48");var subQ1=sQuery(id+"F0.wireOp",EDGE,"E47");var subQ2=sQuery(id+"F0.wireOp",EDGE,"E46");Q17=makeQuery(id+"F10.boolean.opBoolean","TWEAK_FACE",FACE,{"disambiguationData":[OD(2.0)],"derivedFrom":[makeQuery(id+"F10.opExtrude","CAP_FACE",FACE,{"disambiguationData":[OSD([subQ2,subQ1,sQuery(id+"F0.wireOp",EDGE,"E59")])],"isStart":false}),makeQuery(id+"F10.opExtrude","CAP_FACE",FACE,{"disambiguationData":[OSD([subQ2,subQ0,sQuery(id+"F0.wireOp",EDGE,"E64")])],"isStart":false}),makeQuery(id+"F10.opExtrude","CAP_FACE",FACE,{"disambiguationData":[OSD([subQ1,subQ0,sQuery(id+"F0.wireOp",EDGE,"E69")])],"isStart":false})]});}
            var Q18;
            Q18=makeQuery(id+"F10.boolean.opBoolean","COPY",FACE,{"derivedFrom":makeQuery(id+"F10.opExtrude","CAP_FACE",FACE,{"disambiguationData":[OSD([sQuery(id+"F0.wireOp",EDGE,"E68"),sQuery(id+"F0.wireOp",EDGE,"E69"),sQuery(id+"F0.wireOp",EDGE,"E70")])],"isStart":false})});
            var Q19;
            Q19=makeQuery(id+"F10.boolean.opBoolean","COPY",FACE,{"derivedFrom":makeQuery(id+"F10.opExtrude","CAP_FACE",FACE,{"disambiguationData":[OSD([sQuery(id+"F0.wireOp",EDGE,"E44"),sQuery(id+"F0.wireOp",EDGE,"E49"),sQuery(id+"F0.wireOp",EDGE,"E67")])],"isStart":false})});
            var Q20;
            {var subQ0=sQuery(id+"F0.wireOp",EDGE,"E47");Q20=makeQuery(id+"F10.boolean.opBoolean","TWEAK_FACE",FACE,{"disambiguationData":[OD(1.0)],"derivedFrom":[makeQuery(id+"F10.opExtrude","CAP_FACE",FACE,{"disambiguationData":[OSD([sQuery(id+"F0.wireOp",EDGE,"E44"),subQ0,sQuery(id+"F0.wireOp",EDGE,"E60")])],"isStart":false}),makeQuery(id+"F10.opExtrude","CAP_FACE",FACE,{"disambiguationData":[OSD([subQ0,sQuery(id+"F0.wireOp",EDGE,"E49"),sQuery(id+"F0.wireOp",EDGE,"E68")])],"isStart":false})]});}
            var Q21;
            {var subQ0=sQuery(id+"F0.wireOp",EDGE,"E47");Q21=makeQuery(id+"F10.boolean.opBoolean","TWEAK_FACE",FACE,{"disambiguationData":[OD(0.0)],"derivedFrom":[makeQuery(id+"F10.opExtrude","CAP_FACE",FACE,{"disambiguationData":[OSD([sQuery(id+"F0.wireOp",EDGE,"E44"),subQ0,sQuery(id+"F0.wireOp",EDGE,"E60")])],"isStart":false}),makeQuery(id+"F10.opExtrude","CAP_FACE",FACE,{"disambiguationData":[OSD([subQ0,sQuery(id+"F0.wireOp",EDGE,"E49"),sQuery(id+"F0.wireOp",EDGE,"E68")])],"isStart":false})]});}
            extrude(context, id + "F12", {"entities" : qUnion([Q0, Q1, Q2, Q3, Q4, Q5, Q6, Q7, Q8, Q9, Q10, Q11, Q12, Q13, Q14, Q15, Q16, Q17, Q18, Q19, Q20, Q21]), "operationType" : NewBodyOperationType.REMOVE, "oppositeDirection" : true, "depth" : 12.7 * mm});
        }
    });
